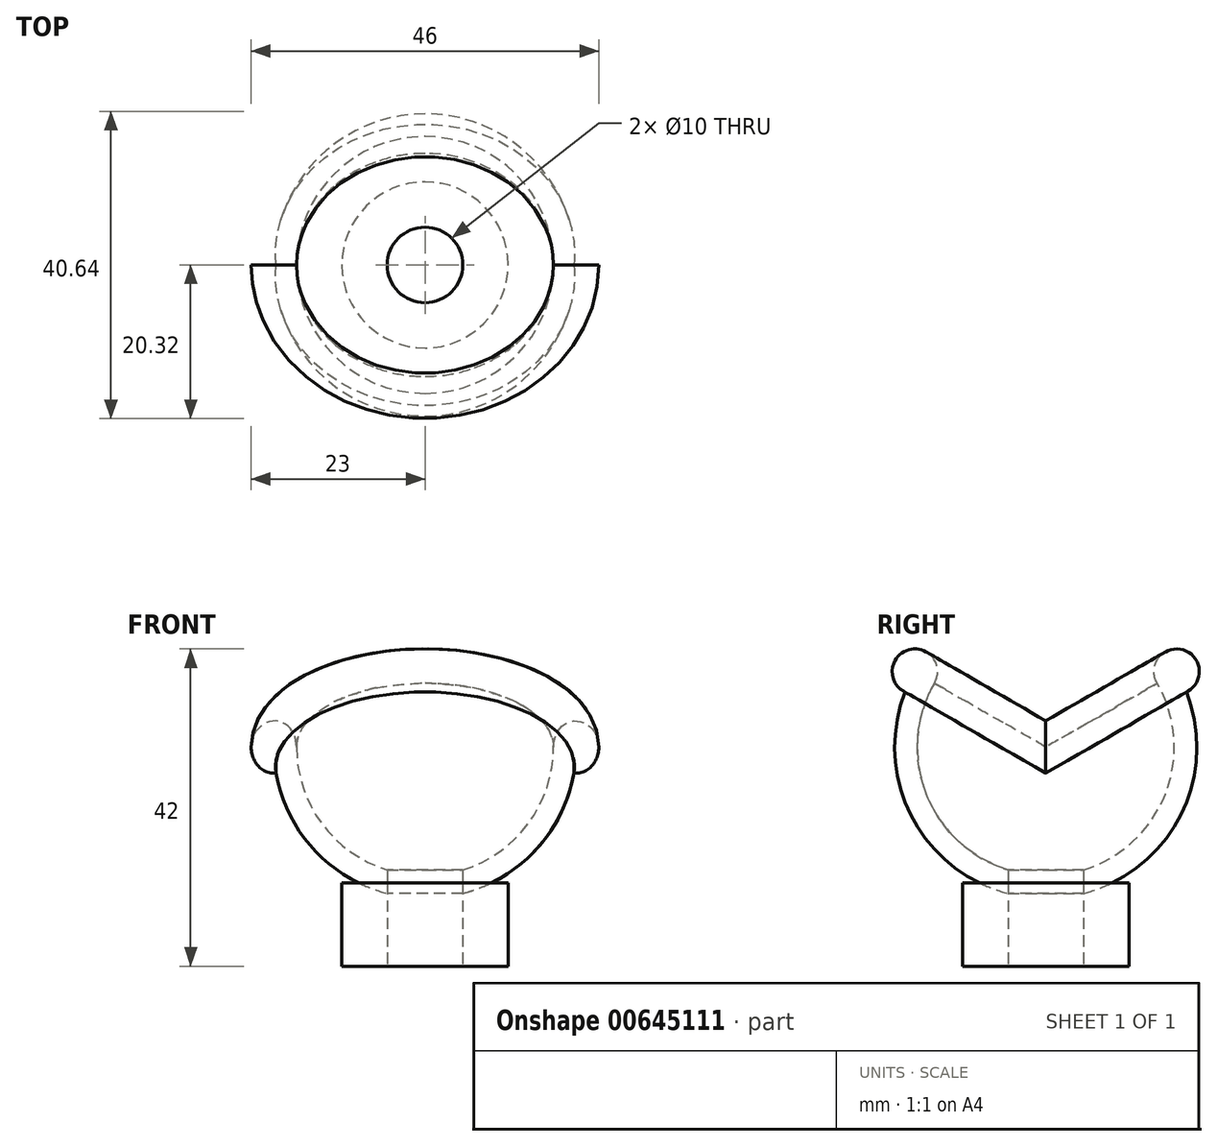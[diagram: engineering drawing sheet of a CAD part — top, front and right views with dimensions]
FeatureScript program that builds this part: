
annotation { "Feature Type Name" : "Feature", "Feature Type Description" : "" }
export const myFeature = defineFeature(function(context is Context, id is Id, definition is map)
    precondition{}
    {
        {
            assignVariable(context, id + "F0", {"name" : "base_height", "anyValue" : 11});
        }
        {
            var Q0;
            Q0=qCreatedBy(makeId("Top.planeOp"),FACE);
            var sketch = newSketch(context, id + "F1", { "sketchPlane" : qUnion([Q0])});
            skCircle(sketch, "E0", {"center": v(0, 0) * mm, "radius": 11 * mm});
            skCircle(sketch, "E1", {"center": v(0, 0) * mm, "radius": 5 * mm});
            skSolve(sketch);
        }
        {
            var Q0;
            Q0=makeQuery(id+"F1.imprint","IMPRINT",FACE,{"disambiguationData":[TD([[makeQuery(id+"F1.imprint","IMPRINT",EDGE,{"derivedFrom":sQuery(id+"F1.wireOp",EDGE,"E0")}),1.0]])]});
            extrude(context, id + "F2", {"entities" : qUnion([Q0]), "depth" : (getVariable(context, 'base_height')) * mm, "offsetDistance" : 25 * mm});
        }
        {
            var Q0;
            Q0=qCreatedBy(makeId("Right.planeOp"),FACE);
            var sketch = newSketch(context, id + "F3", { "sketchPlane" : qUnion([Q0])});
            skCircle(sketch, "E2", {"center": v(0, 29) * mm, "radius": 20 * mm});
            skLineSegment(sketch, "E3", {"start": v(0, 49) * mm, "end": v(0, 9) * mm});
            skLineSegment(sketch, "E4", {"start": v(0, 29) * mm, "end": v(17.32, 39) * mm});
            skLineSegment(sketch, "E5", {"start": v(0, 29) * mm, "end": v(-17.32, 39) * mm});
            skSolve(sketch);
        }
        {
            var Q0;
            {var subQ0=sQuery(id+"F3.wireOp",EDGE,"E3");Q0=makeQuery(id+"F3.imprint","IMPRINT",FACE,{"disambiguationData":[TD([[makeQuery(id+"F3.imprint","IMPRINT",EDGE,{"derivedFrom":subQ0}),1.0]])]});}
            var Q1;
            Q1=sQuery(id+"F3.wireOp",EDGE,"E3");
            revolve(context, id + "F4", {"entities" : qUnion([Q0]), "axis" : qUnion([Q1]), "revolveType" : RevolveType.FULL});
        }
        {
            var Q0;
            {var subQ3=sQuery(id+"F3.wireOp",EDGE,"E4");Q0=makeQuery(id+"F3.imprint","IMPRINT",FACE,{"disambiguationData":[TD([[makeQuery(id+"F3.imprint","IMPRINT",EDGE,{"derivedFrom":subQ3}),1.0]])]});}
            var Q1;
            {var subQ3=sQuery(id+"F3.wireOp",EDGE,"E5");Q1=makeQuery(id+"F3.imprint","IMPRINT",FACE,{"disambiguationData":[TD([[makeQuery(id+"F3.imprint","IMPRINT",EDGE,{"derivedFrom":subQ3}),-1.0]])]});}
            extrude(context, id + "F5", {"entities" : qUnion([Q0, Q1]), "operationType" : NewBodyOperationType.REMOVE, "endBound" : BoundingType.SYMMETRIC, "depth" : 100 * mm, "offsetDistance" : 25 * mm});
        }
        {
            var Q0;
            Q0=makeQuery(id+"F5.boolean.opBoolean","COPY",FACE,{"derivedFrom":makeQuery(id+"F5.opExtrude","SWEPT_FACE",FACE,{"disambiguationData":[OSD([sQuery(id+"F3.wireOp",EDGE,"E5")])]})});
            var Q1;
            Q1=makeQuery(id+"F5.boolean.opBoolean","COPY",FACE,{"derivedFrom":makeQuery(id+"F5.opExtrude","SWEPT_FACE",FACE,{"disambiguationData":[OSD([sQuery(id+"F3.wireOp",EDGE,"E4")])]})});
            var Q2;
            Q2=makeQuery(id+"F2.opExtrude","SWEPT_BODY",BODY,{"disambiguationData":[OSD([sQuery(id+"F1.wireOp",EDGE,"E0"),sQuery(id+"F1.wireOp",EDGE,"E1")])]});
            shell(context, id + "F6", {"entities" : qUnion([Q0, Q1]), "parts" : qUnion([Q2]), "thickness" : 3 * mm});
        }
        {
            var Q0;
            Q0=makeQuery(id+"F1.imprint","IMPRINT",FACE,{"disambiguationData":[TD([[makeQuery(id+"F1.imprint","IMPRINT",EDGE,{"derivedFrom":sQuery(id+"F1.wireOp",EDGE,"E1")}),1.0]])]});
            extrude(context, id + "F7", {"entities" : qUnion([Q0]), "operationType" : NewBodyOperationType.REMOVE, "depth" : 25 * mm, "offsetDistance" : 25 * mm});
        }
        {
            var Q0;
            Q0=qCreatedBy(makeId("Right.planeOp"),FACE);
            var sketch = newSketch(context, id + "F8", { "sketchPlane" : qUnion([Q0])});
            skCircle(sketch, "E6", {"center": v(-17.32, 39) * mm, "radius": 3 * mm});
            skSolve(sketch);
        }
        {
            var Q0;
            Q0=makeQuery(id+"F8.imprint","IMPRINT",FACE,{"disambiguationData":[TD([[makeQuery(id+"F8.imprint","IMPRINT",EDGE,{"derivedFrom":sQuery(id+"F8.wireOp",EDGE,"E6")}),1.0]])]});
            var Q1;
            Q1=makeQuery(id+"F5.boolean.opBoolean","INTERSECT",EDGE,{"derivedFrom":[makeQuery(id+"F4.boolean.opBoolean","SPLIT",FACE,{"disambiguationData":[TD([makeQuery(id+"F2.opExtrude","CAP_FACE",FACE,{"disambiguationData":[OSD([sQuery(id+"F1.wireOp",EDGE,"E0"),sQuery(id+"F1.wireOp",EDGE,"E1")])],"isStart":false})])],"derivedFrom":makeQuery(id+"F4.opRevolve","SWEPT_FACE",FACE,{"disambiguationData":[OSD([sQuery(id+"F3.wireOp",EDGE,"E2")])]})}),makeQuery(id+"F5.opExtrude","SWEPT_FACE",FACE,{"disambiguationData":[OSD([sQuery(id+"F3.wireOp",EDGE,"E5")])]})]});
            var Q2;
            Q2=makeQuery(id+"F5.boolean.opBoolean","INTERSECT",EDGE,{"derivedFrom":[makeQuery(id+"F4.boolean.opBoolean","SPLIT",FACE,{"disambiguationData":[TD([makeQuery(id+"F2.opExtrude","CAP_FACE",FACE,{"disambiguationData":[OSD([sQuery(id+"F1.wireOp",EDGE,"E0"),sQuery(id+"F1.wireOp",EDGE,"E1")])],"isStart":false})])],"derivedFrom":makeQuery(id+"F4.opRevolve","SWEPT_FACE",FACE,{"disambiguationData":[OSD([sQuery(id+"F3.wireOp",EDGE,"E2")])]})}),makeQuery(id+"F5.opExtrude","SWEPT_FACE",FACE,{"disambiguationData":[OSD([sQuery(id+"F3.wireOp",EDGE,"E4")])]})]});
            sweep(context, id + "F9", {"operationType" : NewBodyOperationType.ADD, "profiles" : qUnion([Q0]), "path" : qUnion([Q1, Q2])});
        }
    });
